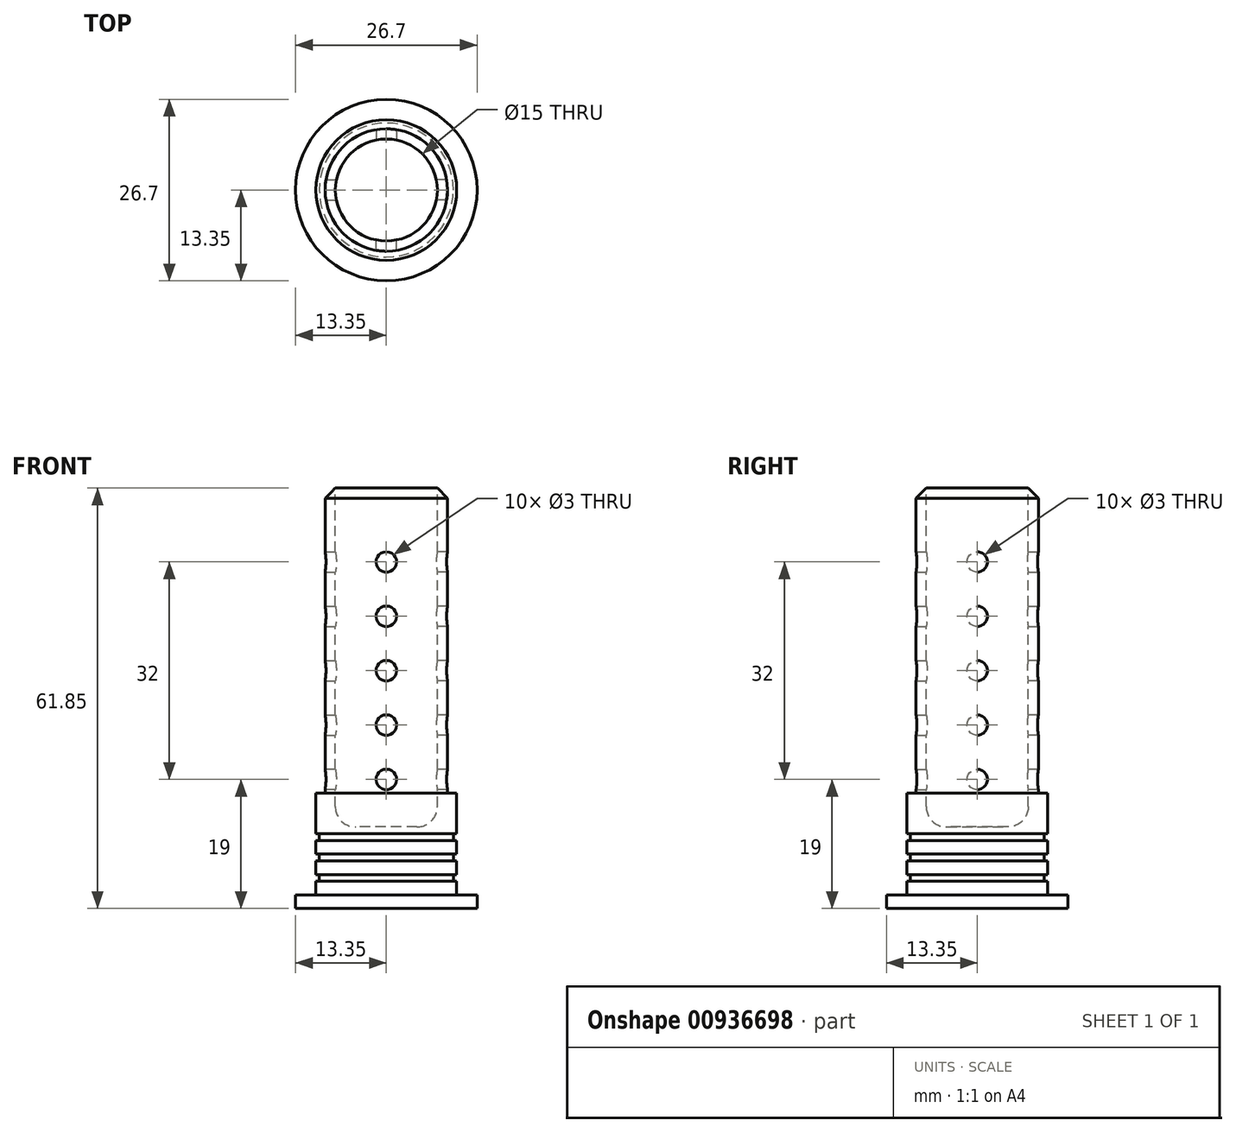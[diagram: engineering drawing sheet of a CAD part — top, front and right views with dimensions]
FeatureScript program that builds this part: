
annotation { "Feature Type Name" : "Feature", "Feature Type Description" : "" }
export const myFeature = defineFeature(function(context is Context, id is Id, definition is map)
    precondition{}
    {
        {
            var Q0;
            Q0=qCreatedBy(makeId("Front.planeOp"),FACE);
            var sketch = newSketch(context, id + "F0", { "sketchPlane" : qUnion([Q0])});
            skLineSegment(sketch, "E0", {"start": v(0, 0) * mm, "end": v(0, 24.32) * mm, "construction": true});
            skLineSegment(sketch, "E1", {"start": v(0, 0) * mm, "end": v(10.35, 0) * mm});
            skLineSegment(sketch, "E2", {"start": v(10.35, 2) * mm, "end": v(10.35, 4) * mm});
            skLineSegment(sketch, "E3", {"start": v(10.35, 62) * mm, "end": v(0, 62) * mm});
            skLineSegment(sketch, "E4", {"start": v(0, 62) * mm, "end": v(0, 0) * mm});
            skLineSegment(sketch, "E5", {"start": v(10.35, 4) * mm, "end": v(9.85, 4) * mm});
            skLineSegment(sketch, "E6", {"start": v(9.85, 4) * mm, "end": v(9.85, 5) * mm});
            skLineSegment(sketch, "E7", {"start": v(9.85, 5) * mm, "end": v(10.35, 5) * mm});
            skLineSegment(sketch, "E8", {"start": v(10.35, 0) * mm, "end": v(13.35, 0) * mm});
            skLineSegment(sketch, "E9", {"start": v(13.35, 0) * mm, "end": v(13.35, 2) * mm});
            skLineSegment(sketch, "E10", {"start": v(13.35, 2) * mm, "end": v(10.35, 2) * mm});
            skLineSegment(sketch, "E11.trimOffspring", {"start": v(10.35, 5) * mm, "end": v(10.35, 7) * mm});
            skLineSegment(sketch, "E12", {"start": v(10.35, 7) * mm, "end": v(9.85, 7) * mm});
            skLineSegment(sketch, "E13", {"start": v(9.85, 7) * mm, "end": v(9.85, 8) * mm});
            skLineSegment(sketch, "E14", {"start": v(9.85, 8) * mm, "end": v(10.35, 8) * mm});
            skLineSegment(sketch, "E15", {"start": v(10.35, 8) * mm, "end": v(10.35, 10) * mm});
            skLineSegment(sketch, "E16", {"start": v(10.35, 10) * mm, "end": v(9.85, 10) * mm});
            skLineSegment(sketch, "E17", {"start": v(9.85, 10) * mm, "end": v(9.85, 11) * mm});
            skLineSegment(sketch, "E18", {"start": v(9.85, 11) * mm, "end": v(10.35, 11) * mm});
            skLineSegment(sketch, "E19.trimOffspring", {"start": v(10.35, 11) * mm, "end": v(10.35, 62) * mm});
            skSolve(sketch);
        }
        {
            var Q0;
            Q0=qSketchRegion(id+"F0",true);
            var Q1;
            Q1=sQuery(id+"F0.wireOp",EDGE,"E0");
            revolve(context, id + "F1", {"surfaceOperationType" : NewSurfaceOperationType.NEW, "entities" : qUnion([Q0]), "axis" : qUnion([Q1]), "revolveType" : RevolveType.FULL});
        }
        {
            var Q0;
            Q0=makeQuery(id+"F1.opRevolve","SWEPT_EDGE",EDGE,{"disambiguationData":[OSD([sQuery(id+"F0.wireOp",EDGE,"E3"),sQuery(id+"F0.wireOp",EDGE,"E19.trimOffspring")])]});
            chamfer(context, id + "F2", {"entities" : qUnion([Q0]), "width" : 3 * mm, "tangentPropagation" : true});
        }
        {
            var Q0;
            Q0=makeQuery(id+"F1.opRevolve","SWEPT_FACE",FACE,{"disambiguationData":[OSD([sQuery(id+"F0.wireOp",EDGE,"E3")])]});
            var sketch = newSketch(context, id + "F3", { "sketchPlane" : qUnion([Q0])});
            skCircle(sketch, "E20", {"center": v(0, 0) * mm, "radius": 7.5 * mm});
            skSolve(sketch);
        }
        {
            var Q0;
            Q0=qSketchRegion(id+"F3",true);
            var Q1;
            Q1=makeQuery(id+"F1.opRevolve","SWEPT_FACE",FACE,{"disambiguationData":[OSD([sQuery(id+"F0.wireOp",EDGE,"E10")])]});
            extrude(context, id + "F4", {"entities" : qUnion([Q0]), "operationType" : NewBodyOperationType.REMOVE, "endBound" : BoundingType.UP_TO_SURFACE, "oppositeDirection" : true, "depth" : 12.9 * mm, "endBoundEntityFace" : qUnion([Q1]), "hasOffset" : true, "offsetDistance" : 10 * mm});
        }
        {
            var Q0;
            Q0=makeQuery(id+"F4.boolean.opBoolean","COPY",EDGE,{"derivedFrom":makeQuery(id+"F4.opExtrude","CAP_EDGE",EDGE,{"disambiguationData":[OSD([sQuery(id+"F3.wireOp",EDGE,"E20")])],"isStart":false})});
            fillet(context, id + "F5", {"entities" : qUnion([Q0]), "radius" : 3 * mm, "tangentPropagation" : true, "allowEdgeOverflow" : false});
        }
        {
            var Q0;
            Q0=qCreatedBy(makeId("Front.planeOp"),FACE);
            var sketch = newSketch(context, id + "F6", { "sketchPlane" : qUnion([Q0])});
            skCircle(sketch, "E21", {"center": v(0, 19) * mm, "radius": 1.5 * mm});
            skCircle(sketch, "E22.0.1.0", {"center": v(0, 27) * mm, "radius": 1.5 * mm});
            skCircle(sketch, "E22.0.2.0", {"center": v(0, 35) * mm, "radius": 1.5 * mm});
            skCircle(sketch, "E22.0.3.0", {"center": v(0, 43) * mm, "radius": 1.5 * mm});
            skCircle(sketch, "E22.0.4.0", {"center": v(0, 51) * mm, "radius": 1.5 * mm});
            skLineSegment(sketch, "E22.direction1", {"start": v(0, 19) * mm, "end": v(25, 19) * mm, "construction": true});
            skLineSegment(sketch, "E22.direction2", {"start": v(0, 19) * mm, "end": v(0, 27) * mm, "construction": true});
            skSolve(sketch);
        }
        {
            var Q0;
            Q0 = qSketchRegion(id + "F6", true);
            extrude(context, id + "F7", {"entities" : qUnion([Q0]), "depth" : 25 * mm, "offsetDistance" : 25 * mm});
        }
        {
            var Q0;
            Q0=qCreatedBy(makeId("Front.planeOp"),FACE);
            var sketch = newSketch(context, id + "F8", { "sketchPlane" : qUnion([Q0])});
            skLineSegment(sketch, "E23", {"start": v(0, 0) * mm, "end": v(0, 103.26) * mm, "construction": true});
            skSolve(sketch);
        }
        {
            var Q0;
            Q0=makeQuery(id+"F7.opExtrude","SWEPT_BODY",BODY,{"disambiguationData":[OSD([sQuery(id+"F6.wireOp",EDGE,"E22.0.1.0")])]});
            var Q1;
            Q1=makeQuery(id+"F7.opExtrude","SWEPT_BODY",BODY,{"disambiguationData":[OSD([sQuery(id+"F6.wireOp",EDGE,"E22.0.2.0")])]});
            var Q2;
            Q2=makeQuery(id+"F7.opExtrude","SWEPT_BODY",BODY,{"disambiguationData":[OSD([sQuery(id+"F6.wireOp",EDGE,"E22.0.3.0")])]});
            var Q3;
            Q3=makeQuery(id+"F7.opExtrude","SWEPT_BODY",BODY,{"disambiguationData":[OSD([sQuery(id+"F6.wireOp",EDGE,"E22.0.4.0")])]});
            var Q4;
            Q4=makeQuery(id+"F7.opExtrude","SWEPT_BODY",BODY,{"disambiguationData":[OSD([sQuery(id+"F6.wireOp",EDGE,"E22.0.5.0")])]});
            var Q5;
            Q5=makeQuery(id+"F7.opExtrude","SWEPT_BODY",BODY,{"disambiguationData":[OSD([sQuery(id+"F6.wireOp",EDGE,"E21")])]});
            var Q6;
            Q6=sQuery(id+"F8.wireOp",EDGE,"E23");
            circularPattern(context, id + "F9", {"operationType" : NewBodyOperationType.REMOVE, "entities" : qUnion([Q0, Q1, Q2, Q3, Q4, Q5]), "axis" : qUnion([Q6]), "angle" : 360 * degree, "instanceCount" : 4, "equalSpace" : true});
        }
        {
            var Q0;
            Q0=makeQuery(id+"F1.opRevolve","SWEPT_FACE",FACE,{"disambiguationData":[OSD([sQuery(id+"F0.wireOp",EDGE,"E10")])]});
            cPlane(context, id + "F10", {"entities" : qUnion([Q0]), "cplaneType" : CPlaneType.OFFSET, "offset" : 60 * mm, "width" : 150 * mm, "height" : 150 * mm});
        }
        {
            var Q0;
            Q0=qCreatedBy(id+"F10.planeOp",FACE);
            var sketch = newSketch(context, id + "F11", { "sketchPlane" : qUnion([Q0])});
            skCircle(sketch, "E24", {"center": v(0, 0) * mm, "radius": 9 * mm});
            skCircle(sketch, "E25", {"center": v(0, 0) * mm, "radius": 12 * mm});
            skCircle(sketch, "E26.0", {"center": v(0, 0) * mm, "radius": 10.35 * mm, "construction": true});
            skCircle(sketch, "E27.0", {"center": v(0, 0) * mm, "radius": 7.5 * mm, "construction": true});
            skSolve(sketch);
        }
        {
            var Q0;
            Q0 = qSketchRegion(id + "F11", true);
            extrude(context, id + "F12", {"entities" : qUnion([Q0]), "operationType" : NewBodyOperationType.REMOVE, "oppositeDirection" : true, "depth" : 45 * mm, "offsetDistance" : 25 * mm});
        }
    });
